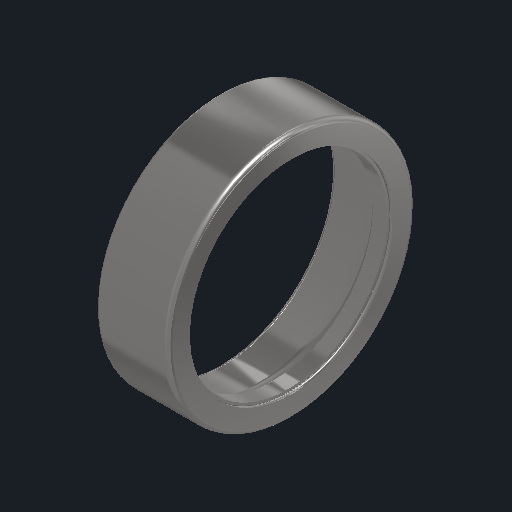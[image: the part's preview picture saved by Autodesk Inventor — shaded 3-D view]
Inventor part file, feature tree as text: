
AUTODESK INVENTOR PART (.ipt)
format: ipt  version: 2022 (Build 260153000, 153)  size: 174,080 bytes
history: native  units: mm (DEFAULTED — no unit token found)
features: revolve x1, sketch x1
ambient origin geometry x8: Origin, YZ Plane, XZ Plane, XY Plane, X Axis, Y Axis, Z Axis, Center Point
bodies: Solid1 (feature_tree)
feature tree (2):
  revolve  "Revolution1"  [1 undecoded]
  sketch  "Sketch_4"  dims[d0=360.0deg]
note: 1 required parameter value undecoded (feature->parameter linkage not recoverable at this tier; creation-order binding heuristic only, values carry confidence <= 0.55)
